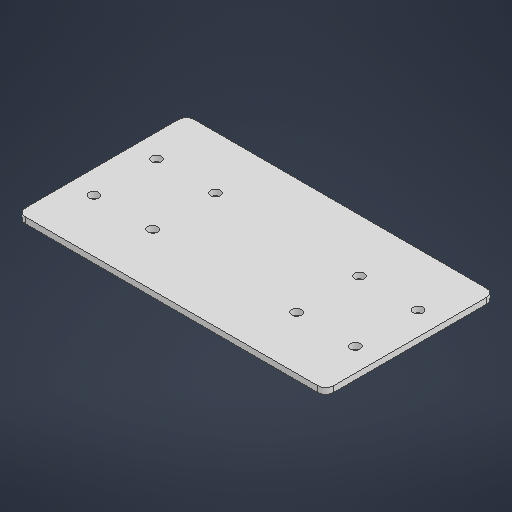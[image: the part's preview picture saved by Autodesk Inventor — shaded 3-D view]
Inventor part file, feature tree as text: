
AUTODESK INVENTOR PART (.ipt)
format: ipt  version: 2025.1 (Build 291241000, 241)  size: 211,456 bytes
history: native  units: mm
features: extrude x1, fillet x1, sketch x1
ambient origin geometry x8: Origin, YZ Plane, XZ Plane, XY Plane, X Axis, Y Axis, Z Axis, Center Point
bodies: Solid1 (feature_tree)
feature tree (3):
  extrude  "Extrusion1"  Depth=86.0mm
  fillet  "Fillet1"  Radius=45.3mm
  sketch  "Sketch1"  dims[d0=157.0mm d1=86.0mm d2=5.0mm d3=5.0mm d4=30.0mm d5=5.0mm d6=5.0mm d7=30.0mm d8=32.0mm d9=5.0mm d10=5.0mm d11=30.0mm d12=5.0mm d13=5.0mm d14=30.0mm d15=32.0mm d16=45.3mm d17=44.0mm d18=45.3mm d19=44.0mm d20=58.0mm d21=3.0mm d22=0.0mm d23=4.0mm]
